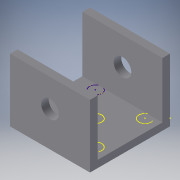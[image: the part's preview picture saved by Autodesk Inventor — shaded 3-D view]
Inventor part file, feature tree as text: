
AUTODESK INVENTOR PART (.ipt)
format: ipt  version: 2016 (Build 200138000, 138)  size: 135,680 bytes
history: native  units: in
note: dims shown in document units (in); Inventor stores cm internally (conversion verified against a paired STEP export)
features: reference x5, extrude x4, sketch x4
ambient origin geometry x8: Origin, YZ Plane, XZ Plane, XY Plane, X Axis, Y Axis, Z Axis, Center Point
bodies: Solid1 (feature_tree)
feature tree (13):
  extrude  "Extrusion1"  Depth=0.637in
  extrude  "Extrusion2"  Depth=0.06in
  extrude  "Extrusion3"  Depth=0.444in TaperAngle=0.0deg
  extrude  "Extrusion4"  Depth=0.444in TaperAngle=0.0deg
  sketch  "Sketch1"  dims[d0=0.637in d1=0.637in]
  sketch  "Sketch2"  dims[d2=0.057in d3=0.0in d4=0.06in]
  sketch  "Sketch3"  dims[d5=0.06in d6=0.444in d7=0.0in]
  sketch  "Sketch4"  dims[d8=0.1406in d9=0.444in d10=0.0in d11=1.0in d12=0.0in]
  reference  "Reference1"
  reference  "Reference2"
  reference  "Reference3"
  reference  "Reference4"
  reference  "Reference5"
